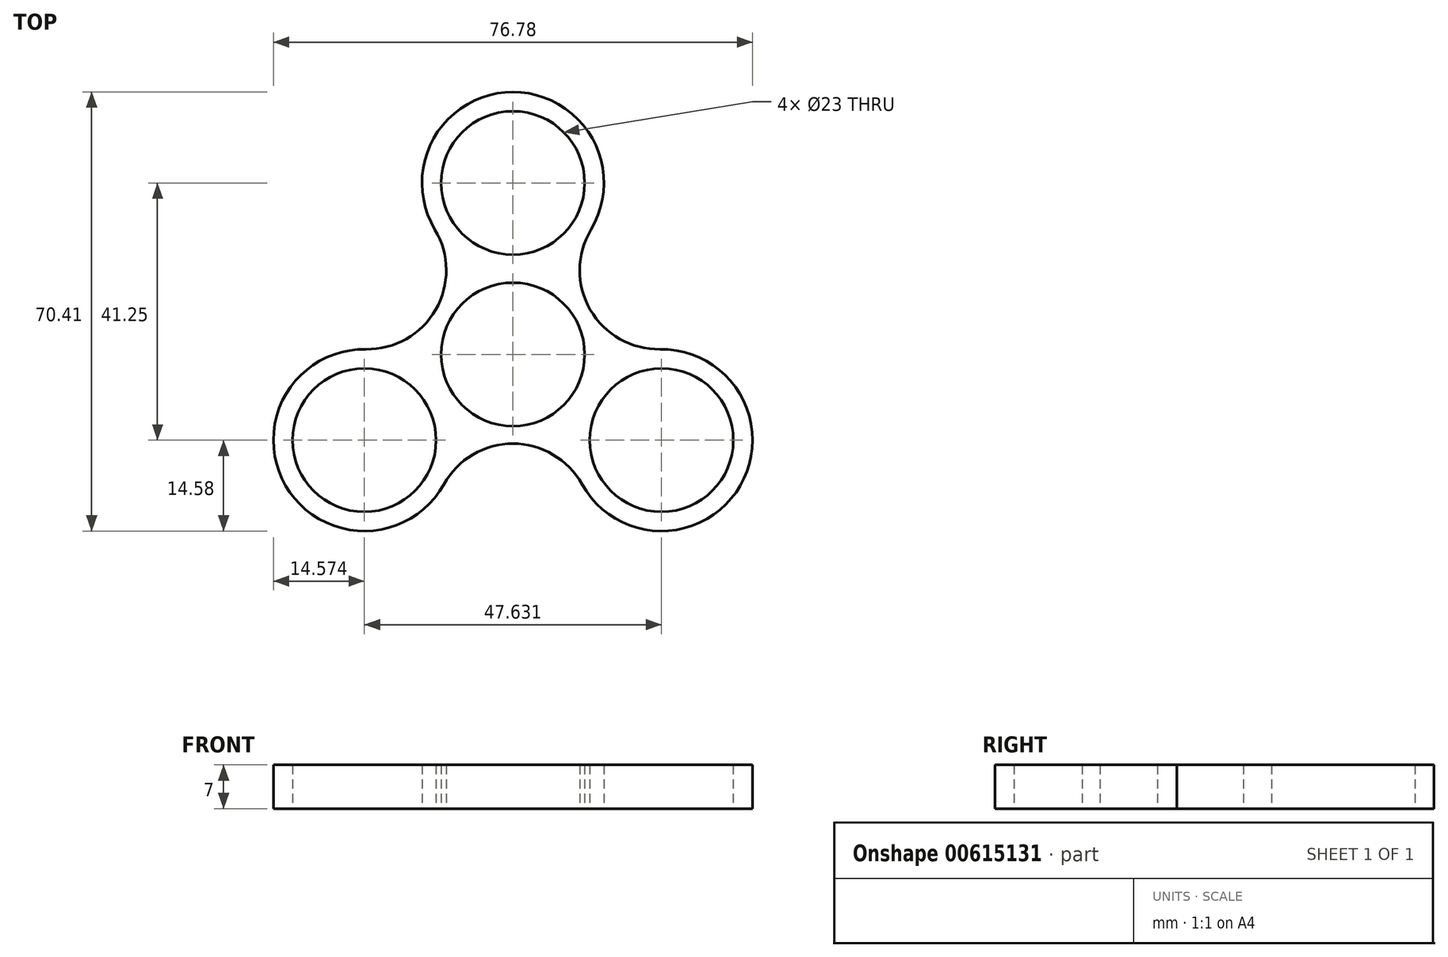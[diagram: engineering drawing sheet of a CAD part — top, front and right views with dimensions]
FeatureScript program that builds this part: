
annotation { "Feature Type Name" : "Feature", "Feature Type Description" : "" }
export const myFeature = defineFeature(function(context is Context, id is Id, definition is map)
    precondition{}
    {
        {
            var Q0;
            Q0=qCreatedBy(makeId("Top.planeOp"),FACE);
            var sketch = newSketch(context, id + "F0", { "sketchPlane" : qUnion([Q0])});
            skCircle(sketch, "E0", {"center": v(0, 0) * mm, "radius": 11.5 * mm});
            skCircle(sketch, "E1", {"center": v(0, 27.5) * mm, "radius": 11.5 * mm});
            skCircle(sketch, "E2.1.1", {"center": v(-23.82, -13.75) * mm, "radius": 11.5 * mm});
            skCircle(sketch, "E2.2.1", {"center": v(23.82, -13.75) * mm, "radius": 11.5 * mm});
            skArc(sketch, "E3", {"start": v(-12.5, 20) * mm, "mid": v(0, 42.08) * mm, "end": v(12.5, 20) * mm});
            skPoint(sketch, "E4.center", {"position": v(0, -10) * mm});
            skPoint(sketch, "E5.center", {"position": v(-0.5, 2.74) * mm});
            skArc(sketch, "E6.1.0", {"start": v(-11.07, -20.83) * mm, "mid": v(-36.44, -21.04) * mm, "end": v(-23.57, 0.83) * mm});
            skArc(sketch, "E6.2.0", {"start": v(23.57, 0.83) * mm, "mid": v(36.44, -21.04) * mm, "end": v(11.07, -20.83) * mm});
            skArc(sketch, "E7", {"start": v(-12.5, 20) * mm, "mid": v(-12.4, 7.15) * mm, "end": v(-23.57, 0.83) * mm});
            skArc(sketch, "E8", {"start": v(-11.07, -20.83) * mm, "mid": v(0, -14.3) * mm, "end": v(11.07, -20.83) * mm});
            skArc(sketch, "E9", {"start": v(23.57, 0.83) * mm, "mid": v(12.4, 7.15) * mm, "end": v(12.5, 20) * mm});
            skSolve(sketch);
        }
        {
            var Q0;
            Q0=makeQuery(id+"F0.imprint","IMPRINT",FACE,{"disambiguationData":[TD([[makeQuery(id+"F0.imprint","IMPRINT",EDGE,{"derivedFrom":sQuery(id+"F0.wireOp",EDGE,"E0")}),-1.0]])]});
            extrude(context, id + "F1", {"entities" : qUnion([Q0]), "depth" : 7 * mm, "offsetDistance" : 25 * mm});
        }
    });
